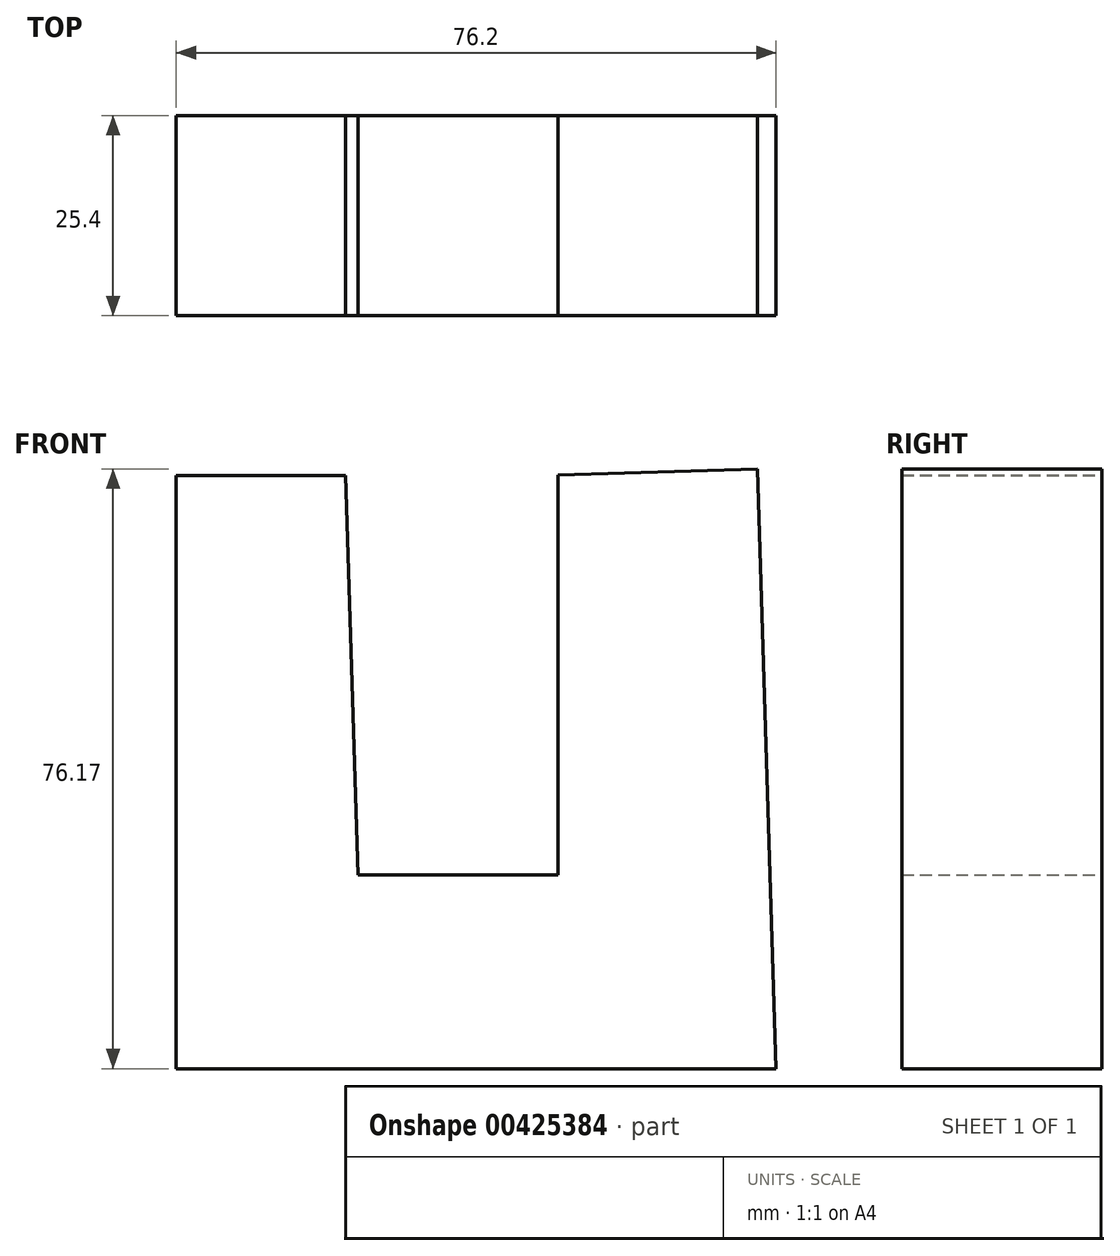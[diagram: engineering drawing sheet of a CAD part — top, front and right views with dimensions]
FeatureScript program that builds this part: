
annotation { "Feature Type Name" : "Feature", "Feature Type Description" : "" }
export const myFeature = defineFeature(function(context is Context, id is Id, definition is map)
    precondition{}
    {
        {
            var Q0;
            Q0=qCreatedBy(makeId("Front.planeOp"),FACE);
            var sketch = newSketch(context, id + "F0", { "sketchPlane" : qUnion([Q0])});
            skLineSegment(sketch, "E0", {"start": v(-35.32, 40.65) * mm, "end": v(-35.32, -35.55) * mm});
            skLineSegment(sketch, "E1", {"start": v(-35.32, -35.55) * mm, "end": v(40.88, -35.55) * mm});
            skLineSegment(sketch, "E2", {"start": v(40.88, -35.55) * mm, "end": v(38.54, 40.62) * mm});
            skLineSegment(sketch, "E3", {"start": v(38.54, 40.62) * mm, "end": v(13.15, 39.84) * mm});
            skLineSegment(sketch, "E4", {"start": v(13.15, 39.84) * mm, "end": v(13.15, -10.96) * mm});
            skLineSegment(sketch, "E5", {"start": v(13.15, -10.96) * mm, "end": v(-12.25, -10.96) * mm});
            skLineSegment(sketch, "E6", {"start": v(-12.25, -10.96) * mm, "end": v(-13.82, 39.81) * mm});
            skLineSegment(sketch, "E7", {"start": v(-13.82, 39.81) * mm, "end": v(-39.22, 39.81) * mm});
            skSolve(sketch);
        }
        {
            var Q0;
            Q0 = qSketchRegion(id + "F0", true);
            extrude(context, id + "F1", {"entities" : qUnion([Q0]), "depth" : 25.4 * mm});
        }
    });
